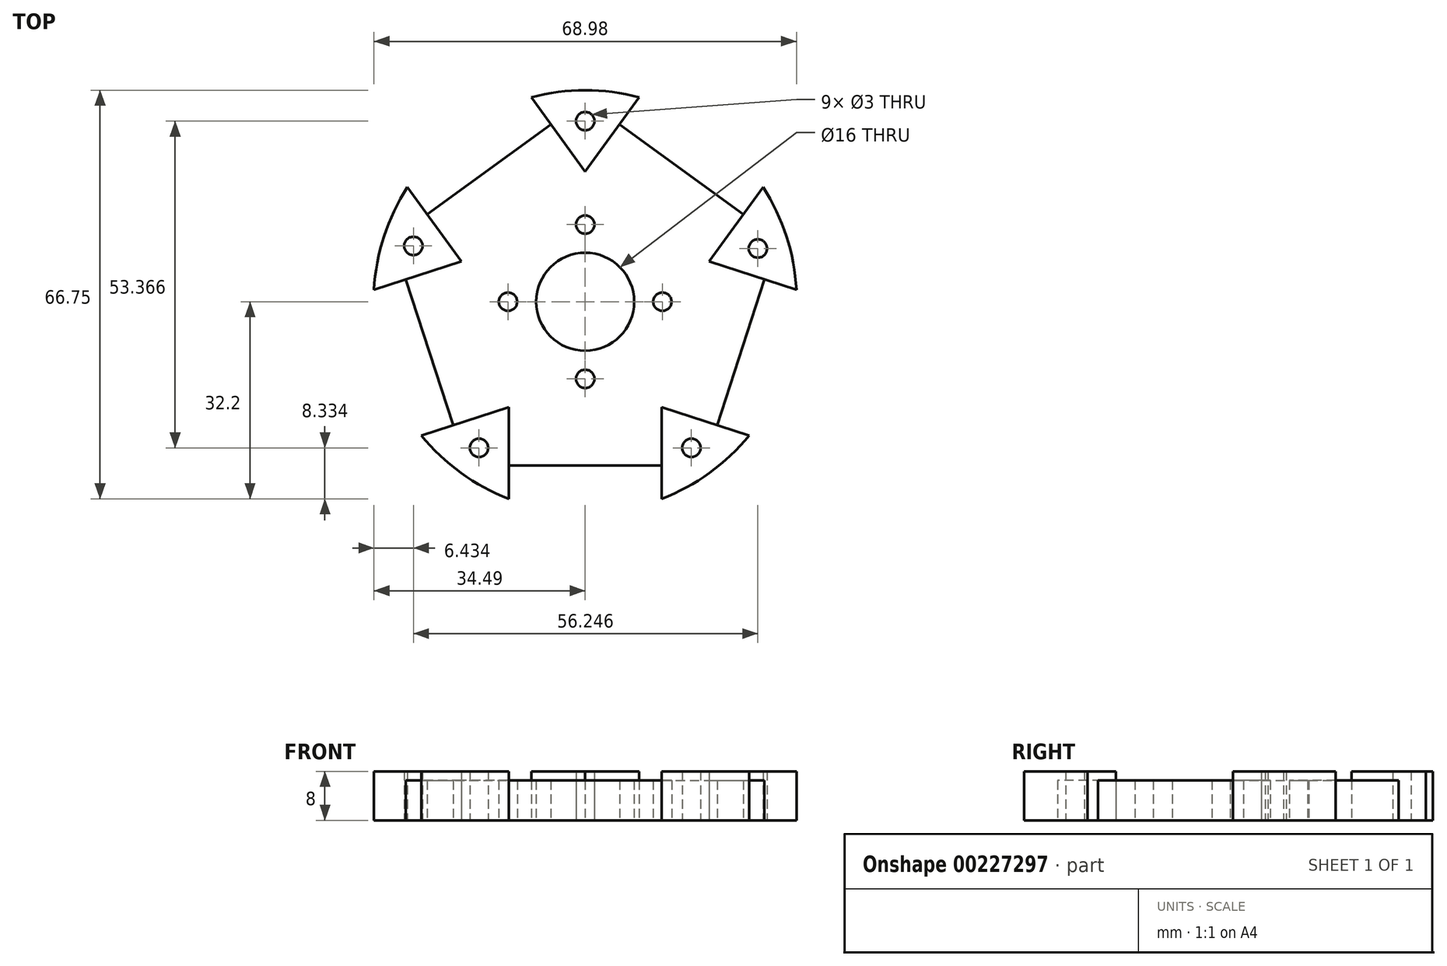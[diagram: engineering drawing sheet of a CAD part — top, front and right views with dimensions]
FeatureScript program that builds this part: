
annotation { "Feature Type Name" : "Feature", "Feature Type Description" : "" }
export const myFeature = defineFeature(function(context is Context, id is Id, definition is map)
    precondition{}
    {
        {
            var Q0;
            Q0=qCreatedBy(makeId("Top.planeOp"),FACE);
            var sketch = newSketch(context, id + "F0", { "sketchPlane" : qUnion([Q0])});
            skCircle(sketch, "E0.cCircle", {"center": v(0, 0) * mm, "radius": 17.2 * mm, "construction": true});
            skLineSegment(sketch, "E0.0", {"start": v(12.5, -17.2) * mm, "end": v(-12.5, -17.2) * mm});
            skLineSegment(sketch, "E0.1", {"start": v(-12.5, -17.2) * mm, "end": v(-20.23, 6.57) * mm});
            skLineSegment(sketch, "E0.2", {"start": v(-20.23, 6.57) * mm, "end": v(0, 21.27) * mm});
            skLineSegment(sketch, "E0.3", {"start": v(0, 21.27) * mm, "end": v(20.23, 6.57) * mm});
            skLineSegment(sketch, "E0.4", {"start": v(20.23, 6.57) * mm, "end": v(12.5, -17.2) * mm});
            skPoint(sketch, "E0.0.midPoint", {"position": v(0, -17.2) * mm});
            skLineSegment(sketch, "E1", {"start": v(9.46, 32.93) * mm, "end": v(8.82, 33.4) * mm});
            skLineSegment(sketch, "E2", {"start": v(-12.5, -17.2) * mm, "end": v(-12.5, -32.2) * mm});
            skLineSegment(sketch, "E3", {"start": v(12.5, -17.2) * mm, "end": v(12.5, -32.2) * mm});
            skLineSegment(sketch, "E4", {"start": v(12.5, -17.2) * mm, "end": v(26.77, -21.84) * mm});
            skLineSegment(sketch, "E5", {"start": v(20.23, 6.57) * mm, "end": v(34.5, 1.94) * mm});
            skLineSegment(sketch, "E6", {"start": v(20.23, 6.57) * mm, "end": v(29.04, 18.7) * mm});
            skLineSegment(sketch, "E7", {"start": v(0, 21.27) * mm, "end": v(8.82, 33.4) * mm});
            skPoint(sketch, "E7.endSnap0", {"position": v(9.46, 32.93) * mm});
            skLineSegment(sketch, "E8", {"start": v(0, 21.27) * mm, "end": v(-8.82, 33.4) * mm});
            skLineSegment(sketch, "E9", {"start": v(-20.23, 6.57) * mm, "end": v(-29.04, 18.7) * mm});
            skLineSegment(sketch, "E10", {"start": v(-20.23, 6.57) * mm, "end": v(-34.5, 1.94) * mm});
            skLineSegment(sketch, "E11", {"start": v(-12.5, -17.2) * mm, "end": v(-26.77, -21.84) * mm});
            skPoint(sketch, "E12.start.orphan", {"position": v(-10.11, 13.92) * mm});
            skPoint(sketch, "E13.start.orphan", {"position": v(10.11, 13.92) * mm});
            skPoint(sketch, "E14.start.orphan", {"position": v(16.36, -5.32) * mm});
            skPoint(sketch, "E15.start.orphan", {"position": v(-16.36, -5.32) * mm});
            skArc(sketch, "E16", {"start": v(-29.04, 18.7) * mm, "mid": v(-32.85, 10.68) * mm, "end": v(-34.5, 1.94) * mm});
            skPoint(sketch, "E17.orphan", {"position": v(0, 39.8) * mm});
            skArc(sketch, "E18.trimOffspring", {"start": v(8.82, 33.4) * mm, "mid": v(0, 34.55) * mm, "end": v(-8.82, 33.4) * mm});
            skArc(sketch, "E19.trimOffspring", {"start": v(34.5, 1.94) * mm, "mid": v(32.85, 10.68) * mm, "end": v(29.04, 18.7) * mm});
            skArc(sketch, "E20.trimOffspring", {"start": v(-26.77, -21.84) * mm, "mid": v(-20.3, -27.95) * mm, "end": v(-12.5, -32.2) * mm});
            skArc(sketch, "E21.trimOffspring", {"start": v(12.5, -32.2) * mm, "mid": v(20.3, -27.95) * mm, "end": v(26.77, -21.84) * mm});
            skCircle(sketch, "E22", {"center": v(0, 0) * mm, "radius": 8 * mm});
            skLineSegment(sketch, "E23", {"start": v(-32.85, 10.68) * mm, "end": v(0, 0) * mm, "construction": true});
            skLineSegment(sketch, "E24", {"start": v(0, 34.55) * mm, "end": v(0, 0) * mm, "construction": true});
            skLineSegment(sketch, "E25", {"start": v(34.61, 10.68) * mm, "end": v(0, 0) * mm, "construction": true});
            skPoint(sketch, "E25.startSnap0", {"position": v(32.85, 10.68) * mm});
            skLineSegment(sketch, "E26", {"start": v(20.3, -27.95) * mm, "end": v(0, 0) * mm, "construction": true});
            skLineSegment(sketch, "E27", {"start": v(0, 0) * mm, "end": v(-20.3, -27.95) * mm, "construction": true});
            skCircle(sketch, "E28", {"center": v(0, 0) * mm, "radius": 29.5 * mm, "construction": true});
            skCircle(sketch, "E29", {"center": v(-28.06, 9.12) * mm, "radius": 1.5 * mm});
            skCircle(sketch, "E30", {"center": v(-17.34, -23.87) * mm, "radius": 1.5 * mm});
            skCircle(sketch, "E31", {"center": v(17.34, -23.87) * mm, "radius": 1.5 * mm});
            skCircle(sketch, "E32", {"center": v(28.19, 8.7) * mm, "radius": 1.5 * mm});
            skCircle(sketch, "E33", {"center": v(0, 29.5) * mm, "radius": 1.5 * mm});
            skLineSegment(sketch, "E34", {"start": v(0, 8) * mm, "end": v(0, 17.2) * mm});
            skLineSegment(sketch, "E35", {"start": v(-8, 0) * mm, "end": v(-17.2, 0) * mm, "construction": true});
            skLineSegment(sketch, "E36", {"start": v(0, -8) * mm, "end": v(0, -17.2) * mm, "construction": true});
            skLineSegment(sketch, "E37", {"start": v(8, 0) * mm, "end": v(17.2, 0) * mm, "construction": true});
            skCircle(sketch, "E38", {"center": v(0, 12.6) * mm, "radius": 1.5 * mm});
            skCircle(sketch, "E39", {"center": v(-12.6, 0) * mm, "radius": 1.5 * mm});
            skCircle(sketch, "E40", {"center": v(0, -12.6) * mm, "radius": 1.5 * mm});
            skCircle(sketch, "E41", {"center": v(12.6, 0) * mm, "radius": 1.5 * mm});
            skLineSegment(sketch, "E42", {"start": v(0, 12.6) * mm, "end": v(12.6, 0) * mm, "construction": true});
            skLineSegment(sketch, "E43", {"start": v(-12.6, 0) * mm, "end": v(0, -12.6) * mm, "construction": true});
            skLineSegment(sketch, "E44", {"start": v(6.3, 6.3) * mm, "end": v(-6.3, -6.3) * mm, "construction": true});
            skLineSegment(sketch, "E45", {"start": v(-6.3, -6.3) * mm, "end": v(-12.17, -12.17) * mm, "construction": true});
            skLineSegment(sketch, "E46", {"start": v(0, 0) * mm, "end": v(12.17, 12.17) * mm, "construction": true});
            skLineSegment(sketch, "E47", {"start": v(-29.28, 3.63) * mm, "end": v(-21.55, -20.15) * mm});
            skLineSegment(sketch, "E48", {"start": v(-12.5, -26.72) * mm, "end": v(12.5, -26.72) * mm});
            skLineSegment(sketch, "E49", {"start": v(21.55, -20.15) * mm, "end": v(29.28, 3.63) * mm});
            skLineSegment(sketch, "E50", {"start": v(-25.82, 14.27) * mm, "end": v(-5.6, 28.96) * mm});
            skLineSegment(sketch, "E51", {"start": v(5.6, 28.96) * mm, "end": v(25.82, 14.27) * mm});
            skPoint(sketch, "E52.start.orphan", {"position": v(18.93, 26.05) * mm});
            skSolve(sketch);
        }
        {
            var Q0;
            Q0=makeQuery(id+"F0.imprint","IMPRINT",FACE,{"disambiguationData":[TD([[makeQuery(id+"F0.imprint","IMPRINT",EDGE,{"derivedFrom":sQuery(id+"F0.wireOp",EDGE,"E9")}),1.0]])]});
            var Q1;
            Q1=makeQuery(id+"F0.imprint","IMPRINT",FACE,{"disambiguationData":[TD([[makeQuery(id+"F0.imprint","IMPRINT",EDGE,{"derivedFrom":sQuery(id+"F0.wireOp",EDGE,"E7")}),1.0]])]});
            var Q2;
            Q2=makeQuery(id+"F0.imprint","IMPRINT",FACE,{"disambiguationData":[TD([[makeQuery(id+"F0.imprint","IMPRINT",EDGE,{"derivedFrom":sQuery(id+"F0.wireOp",EDGE,"E5")}),1.0]])]});
            var Q3;
            Q3=makeQuery(id+"F0.imprint","IMPRINT",FACE,{"disambiguationData":[TD([[makeQuery(id+"F0.imprint","IMPRINT",EDGE,{"derivedFrom":sQuery(id+"F0.wireOp",EDGE,"E3")}),1.0]])]});
            var Q4;
            Q4=makeQuery(id+"F0.imprint","IMPRINT",FACE,{"disambiguationData":[TD([[makeQuery(id+"F0.imprint","IMPRINT",EDGE,{"derivedFrom":sQuery(id+"F0.wireOp",EDGE,"E2")}),-1.0]])]});
            extrude(context, id + "F1", {"entities" : qUnion([Q0, Q1, Q2, Q3, Q4]), "depth" : 8 * mm});
        }
        {
            var Q0;
            Q0=makeQuery(id+"F0.imprint","IMPRINT",FACE,{"disambiguationData":[TD([[makeQuery(id+"F0.imprint","IMPRINT",EDGE,{"derivedFrom":sQuery(id+"F0.wireOp",EDGE,"E0.0")}),1.0]])]});
            var Q1;
            Q1=makeQuery(id+"F0.imprint","IMPRINT",FACE,{"disambiguationData":[TD([[makeQuery(id+"F0.imprint","IMPRINT",EDGE,{"derivedFrom":sQuery(id+"F0.wireOp",EDGE,"E0.1")}),1.0]])]});
            var Q2;
            Q2=makeQuery(id+"F0.imprint","IMPRINT",FACE,{"disambiguationData":[TD([[makeQuery(id+"F0.imprint","IMPRINT",EDGE,{"derivedFrom":sQuery(id+"F0.wireOp",EDGE,"E0.2")}),1.0]])]});
            var Q3;
            Q3=makeQuery(id+"F0.imprint","IMPRINT",FACE,{"disambiguationData":[TD([[makeQuery(id+"F0.imprint","IMPRINT",EDGE,{"derivedFrom":sQuery(id+"F0.wireOp",EDGE,"E0.3")}),1.0]])]});
            var Q4;
            Q4=makeQuery(id+"F0.imprint","IMPRINT",FACE,{"disambiguationData":[TD([[makeQuery(id+"F0.imprint","IMPRINT",EDGE,{"derivedFrom":sQuery(id+"F0.wireOp",EDGE,"E0.0")}),-1.0]])]});
            var Q5;
            Q5=makeQuery(id+"F0.imprint","IMPRINT",FACE,{"disambiguationData":[TD([[makeQuery(id+"F0.imprint","IMPRINT",EDGE,{"derivedFrom":sQuery(id+"F0.wireOp",EDGE,"E0.4")}),1.0]])]});
            extrude(context, id + "F2", {"entities" : qUnion([Q0, Q1, Q2, Q3, Q4, Q5]), "depth" : 6.5 * mm});
        }
    });
